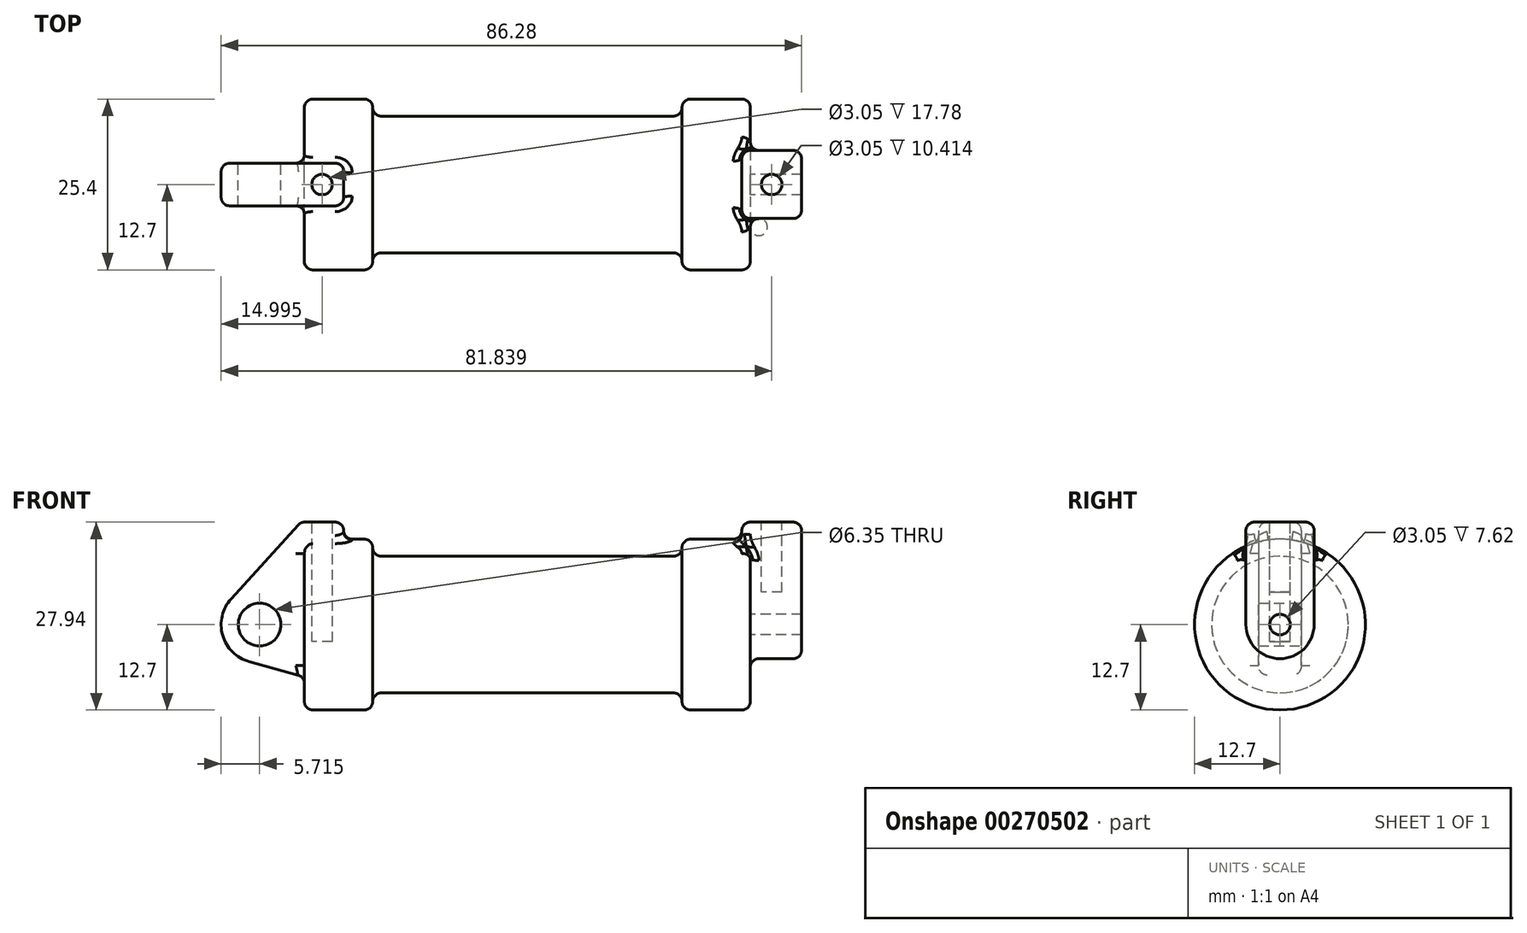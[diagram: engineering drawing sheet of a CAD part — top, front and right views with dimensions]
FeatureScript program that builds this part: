
annotation { "Feature Type Name" : "Feature", "Feature Type Description" : "" }
export const myFeature = defineFeature(function(context is Context, id is Id, definition is map)
    precondition{}
    {
        {
            var Q0;
            Q0=qCreatedBy(makeId("Front.planeOp"),FACE);
            var sketch = newSketch(context, id + "F0", { "sketchPlane" : qUnion([Q0])});
            skLineSegment(sketch, "E0", {"start": v(0, 0) * mm, "end": v(0, 12.7) * mm});
            skLineSegment(sketch, "E1", {"start": v(0, 12.7) * mm, "end": v(10.16, 12.7) * mm});
            skLineSegment(sketch, "E2", {"start": v(10.16, 12.7) * mm, "end": v(10.16, 10.16) * mm});
            skLineSegment(sketch, "E3", {"start": v(10.16, 10.16) * mm, "end": v(56.13, 10.16) * mm});
            skLineSegment(sketch, "E4", {"start": v(56.13, 10.16) * mm, "end": v(56.13, 12.7) * mm});
            skLineSegment(sketch, "E5", {"start": v(56.13, 12.7) * mm, "end": v(66.3, 12.7) * mm});
            skLineSegment(sketch, "E6", {"start": v(66.3, 12.7) * mm, "end": v(66.3, 0) * mm});
            skLineSegment(sketch, "E7", {"start": v(66.3, 0) * mm, "end": v(0, 0) * mm});
            skLineSegment(sketch, "E8", {"start": v(5.84, 15.24) * mm, "end": v(-0.5, 15.24) * mm});
            skLineSegment(sketch, "E9", {"start": v(-0.5, 15.24) * mm, "end": v(-10.88, 3.85) * mm});
            skLineSegment(sketch, "E10", {"start": v(0, 0) * mm, "end": v(-6.65, 0) * mm});
            skCircle(sketch, "E11", {"center": v(-6.65, 0) * mm, "radius": 5.72 * mm});
            skCircle(sketch, "E12", {"center": v(-6.65, 0) * mm, "radius": 3.18 * mm});
            skLineSegment(sketch, "E13", {"start": v(5.84, 15.24) * mm, "end": v(5.84, -9.4) * mm});
            skLineSegment(sketch, "E14", {"start": v(5.84, -9.4) * mm, "end": v(-8.18, -5.5) * mm});
            skSolve(sketch);
        }
        {
            var Q0;
            {var subQ0=sQuery(id+"F0.wireOp",EDGE,"E2");Q0=makeQuery(id+"F0.imprint","IMPRINT",FACE,{"disambiguationData":[TD([[makeQuery(id+"F0.imprint","IMPRINT",EDGE,{"derivedFrom":subQ0}),-1.0]])]});}
            var Q1;
            {var subQ0=sQuery(id+"F0.wireOp",EDGE,"E0");Q1=makeQuery(id+"F0.imprint","IMPRINT",FACE,{"disambiguationData":[TD([[makeQuery(id+"F0.imprint","IMPRINT",EDGE,{"derivedFrom":subQ0}),-1.0]])]});}
            var Q2;
            Q2=sQuery(id+"F0.wireOp",EDGE,"E7");
            revolve(context, id + "F1", {"entities" : qUnion([Q0, Q1]), "axis" : qUnion([Q2]), "revolveType" : RevolveType.FULL});
        }
        {
            var Q0;
            {var subQ0=sQuery(id+"F0.wireOp",EDGE,"E0");Q0=makeQuery(id+"F0.imprint","IMPRINT",FACE,{"disambiguationData":[TD([[makeQuery(id+"F0.imprint","IMPRINT",EDGE,{"derivedFrom":subQ0}),-1.0]])]});}
            var Q1;
            {var subQ3=sQuery(id+"F0.wireOp",EDGE,"E0");Q1=makeQuery(id+"F0.imprint","IMPRINT",FACE,{"disambiguationData":[TD([[makeQuery(id+"F0.imprint","IMPRINT",EDGE,{"derivedFrom":subQ3}),1.0]])]});}
            var Q2;
            {var subQ0=sQuery(id+"F0.wireOp",EDGE,"E14");Q2=makeQuery(id+"F0.imprint","IMPRINT",FACE,{"disambiguationData":[TD([[makeQuery(id+"F0.imprint","IMPRINT",EDGE,{"derivedFrom":subQ0}),-1.0]])]});}
            var Q3;
            {var subQ4=sQuery(id+"F0.wireOp",EDGE,"E12");Q3=makeQuery(id+"F0.imprint","IMPRINT",FACE,{"disambiguationData":[TD([[makeQuery(id+"F0.imprint","IMPRINT",EDGE,{"derivedFrom":subQ4}),-1.0]])]});}
            extrude(context, id + "F2", {"entities" : qUnion([Q0, Q1, Q2, Q3]), "operationType" : NewBodyOperationType.ADD, "endBound" : BoundingType.SYMMETRIC, "depth" : 6.35 * mm});
        }
        {
            var Q0;
            Q0=makeQuery(id+"F1.opRevolve","SWEPT_FACE",FACE,{"disambiguationData":[OSD([sQuery(id+"F0.wireOp",EDGE,"E6")])]});
            var sketch = newSketch(context, id + "F3", { "sketchPlane" : qUnion([Q0])});
            skCircle(sketch, "E15", {"center": v(0, 0) * mm, "radius": 1.52 * mm});
            skCircle(sketch, "E16", {"center": v(0, 0) * mm, "radius": 5.07 * mm});
            skLineSegment(sketch, "E17", {"start": v(-5.07, 0) * mm, "end": v(-5.07, 15.24) * mm});
            skLineSegment(sketch, "E18", {"start": v(5.07, 0) * mm, "end": v(5.07, 15.24) * mm});
            skLineSegment(sketch, "E19", {"start": v(-5.07, 15.24) * mm, "end": v(5.07, 15.24) * mm});
            skSolve(sketch);
        }
        {
            var Q0;
            Q0 = qSketchRegion(id + "F3", true);
            extrude(context, id + "F4", {"entities" : qUnion([Q0]), "operationType" : NewBodyOperationType.ADD, "depth" : 7.62 * mm, "hasSecondDirection" : true, "secondDirectionOppositeDirection" : true, "secondDirectionDepth" : 1.27 * mm});
        }
        {
            var Q0;
            Q0=makeQuery(id+"F2.opExtrude","SWEPT_FACE",FACE,{"disambiguationData":[OSD([sQuery(id+"F0.wireOp",EDGE,"E8")])]});
            var sketch = newSketch(context, id + "F5", { "sketchPlane" : qUnion([Q0])});
            skCircle(sketch, "E20", {"center": v(2.63, 0) * mm, "radius": 1.52 * mm});
            skPoint(sketch, "E20.centerSnap0", {"position": v(-0.5, 0) * mm});
            skSolve(sketch);
        }
        {
            var Q0;
            Q0 = qSketchRegion(id + "F5", true);
            extrude(context, id + "F6", {"entities" : qUnion([Q0]), "operationType" : NewBodyOperationType.REMOVE, "oppositeDirection" : true, "depth" : 17.78 * mm});
        }
        {
            var Q0;
            Q0=makeQuery(id+"F4.opExtrude","SWEPT_FACE",FACE,{"disambiguationData":[OSD([sQuery(id+"F3.wireOp",EDGE,"E19")])]});
            var sketch = newSketch(context, id + "F7", { "sketchPlane" : qUnion([Q0])});
            skCircle(sketch, "E21", {"center": v(69.47, 0) * mm, "radius": 1.52 * mm});
            skSolve(sketch);
        }
        {
            var Q0;
            Q0=makeQuery(id+"F7.imprint","IMPRINT",FACE,{"disambiguationData":[TD([[makeQuery(id+"F7.imprint","IMPRINT",EDGE,{"derivedFrom":sQuery(id+"F7.wireOp",EDGE,"E21")}),1.0]])]});
            extrude(context, id + "F8", {"entities" : qUnion([Q0]), "operationType" : NewBodyOperationType.REMOVE, "oppositeDirection" : true, "depth" : 10.4 * mm});
        }
        {
            var Q0;
            Q0=makeQuery(id+"F1.opRevolve","SWEPT_FACE",FACE,{"disambiguationData":[OSD([sQuery(id+"F0.wireOp",EDGE,"E0")])]});
            var Q1;
            Q1=makeQuery(id+"F2.opExtrude","SWEPT_FACE",FACE,{"disambiguationData":[OSD([sQuery(id+"F0.wireOp",EDGE,"E9")])]});
            var Q2;
            Q2=makeQuery(id+"F2.opExtrude","SWEPT_FACE",FACE,{"disambiguationData":[OSD([sQuery(id+"F0.wireOp",EDGE,"E11")])]});
            var Q3;
            Q3=makeQuery(id+"F1.opRevolve","SWEPT_FACE",FACE,{"disambiguationData":[OSD([sQuery(id+"F0.wireOp",EDGE,"E1")])]});
            var Q4;
            Q4=makeQuery(id+"F1.opRevolve","SWEPT_FACE",FACE,{"disambiguationData":[OSD([sQuery(id+"F0.wireOp",EDGE,"E5")])]});
            var Q5;
            Q5=makeQuery(id+"F4.opExtrude","SWEPT_FACE",FACE,{"disambiguationData":[OSD([sQuery(id+"F3.wireOp",EDGE,"E17")])]});
            var Q6;
            Q6=makeQuery(id+"F4.opExtrude","CAP_EDGE",EDGE,{"disambiguationData":[OSD([sQuery(id+"F3.wireOp",EDGE,"E16")])],"isStart":false});
            var Q7;
            Q7=makeQuery(id+"F4.boolean.opBoolean","SPLIT",FACE,{"disambiguationData":[TD([makeQuery(id+"F1.opRevolve","SWEPT_FACE",FACE,{"disambiguationData":[OSD([sQuery(id+"F0.wireOp",EDGE,"E5")])]})])],"derivedFrom":makeQuery(id+"F1.opRevolve","SWEPT_FACE",FACE,{"disambiguationData":[OSD([sQuery(id+"F0.wireOp",EDGE,"E6")])]})});
            var Q8;
            Q8=makeQuery(id+"F4.opExtrude","SWEPT_FACE",FACE,{"disambiguationData":[OSD([sQuery(id+"F3.wireOp",EDGE,"E18")])]});
            var Q9;
            Q9=makeQuery(id+"F1.opRevolve","SWEPT_FACE",FACE,{"disambiguationData":[OSD([sQuery(id+"F0.wireOp",EDGE,"E4")])]});
            var Q10;
            Q10=makeQuery(id+"F1.opRevolve","SWEPT_FACE",FACE,{"disambiguationData":[OSD([sQuery(id+"F0.wireOp",EDGE,"E2")])]});
            var Q11;
            Q11=makeQuery(id+"F1.opRevolve","SWEPT_EDGE",EDGE,{"disambiguationData":[OSD([sQuery(id+"F0.wireOp",EDGE,"E3"),sQuery(id+"F0.wireOp",EDGE,"E4")])]});
            var Q12;
            Q12=makeQuery(id+"F2.opExtrude","SWEPT_FACE",FACE,{"disambiguationData":[OSD([sQuery(id+"F0.wireOp",EDGE,"E13")])]});
            var Q13;
            Q13=makeQuery(id+"F4.opExtrude","CAP_FACE",FACE,{"disambiguationData":[OSD([sQuery(id+"F3.wireOp",EDGE,"E15"),sQuery(id+"F3.wireOp",EDGE,"E16"),sQuery(id+"F3.wireOp",EDGE,"E17"),sQuery(id+"F3.wireOp",EDGE,"E18"),sQuery(id+"F3.wireOp",EDGE,"E19")])],"isStart":true});
            var Q14;
            Q14=makeQuery(id+"F4.opExtrude","CAP_EDGE",EDGE,{"disambiguationData":[OSD([sQuery(id+"F3.wireOp",EDGE,"E19")])],"isStart":false});
            var Q15;
            Q15=makeQuery(id+"F2.opExtrude","CAP_EDGE",EDGE,{"disambiguationData":[OSD([sQuery(id+"F0.wireOp",EDGE,"E8")])],"isStart":false});
            var Q16;
            Q16=makeQuery(id+"F2.opExtrude","CAP_EDGE",EDGE,{"disambiguationData":[OSD([sQuery(id+"F0.wireOp",EDGE,"E8")])],"isStart":true});
            var Q17;
            Q17=makeQuery(id+"F2.opExtrude","SWEPT_EDGE",EDGE,{"disambiguationData":[OSD([sQuery(id+"F0.wireOp",EDGE,"E8"),sQuery(id+"F0.wireOp",EDGE,"E9")])]});
            fillet(context, id + "F9", {"entities" : qUnion([Q0, Q1, Q2, Q3, Q4, Q5, Q6, Q7, Q8, Q9, Q10, Q11, Q12, Q13, Q14, Q15, Q16, Q17]), "radius" : 1.27 * mm, "tangentPropagation" : true, "allowEdgeOverflow" : false});
        }
    });
